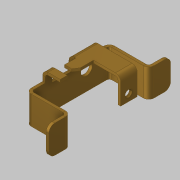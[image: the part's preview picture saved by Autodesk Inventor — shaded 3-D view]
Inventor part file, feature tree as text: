
AUTODESK INVENTOR PART (.ipt)
format: ipt  version: 2019 (Build 230136000, 136)  size: 312,832 bytes
history: native  units: mm
features: sheet_metal_op x9, sketch x9, other x6, extrude x3, hole x2, plane x2, chamfer x1
ambient origin geometry x8: Origin, YZ Plane, XZ Plane, XY Plane, X Axis, Y Axis, Z Axis, Center Point
bodies: Solid1 (feature_tree)
feature tree (32):
  sheet_metal_op  "Contour Flange1"
  chamfer  "Corner Round1"
  hole  "Hole1"  [1 undecoded]
  plane  "Work Plane1"
  sheet_metal_op  "Contour Flange2"
  plane  "Work Plane2"
  sheet_metal_op  "Contour Flange3"
  hole  "Hole2"  [1 undecoded]
  extrude  "Extrusion1"  Depth=3.0mm
  extrude  "Extrusion2"  Depth=6.0mm
  extrude  "Extrusion3"  Depth=32.0mm
  other  "Corner Chamfer1"
  other  "Definición del lado A"
  sketch  "Sketch1"  dims[d0=22.0mm d1=45.0mm]
  other  "Plate1"
  sheet_metal_op  "Bend1"
  sheet_metal_op  "Corner1"
  sketch  "Sketch2"  dims[d4=3.0mm d5=3.0mm]
  sketch  "Sketch5"  dims[d6=1.5mm d7=6.0mm]
  other  "Plate2"
  sheet_metal_op  "Bend2"
  sheet_metal_op  "Corner2"
  sketch  "Sketch6"  dims[d8=3.0mm d9=32.0mm]
  other  "Plate3"
  sheet_metal_op  "Bend3"
  sheet_metal_op  "Corner3"
  sketch  "Sketch7"  dims[d10=3.0mm]
  sketch  "Sketch8"  dims[d11=0.5mm]
  sketch  "Sketch9"  dims[d12=12.0mm]
  sketch  "Sketch10"  dims[d13=3.0mm d14=3.0mm d15=7.0mm d16=13.0mm d17=6.0mm d18=4.0mm d19=2.0mm d20=90.0deg d21=3.0mm d22=20.594885mm d23=22.0mm d25=-19.0mm d26=12.0mm d27=20.0mm d28=3.0mm d29=1.5mm d30=6.0mm d31=3.0mm d32=8.0mm d33=3.0mm d34=3.0mm d35=12.0mm d36=3.0mm d37=3.0mm d38=-49.0mm d39=12.0mm d41=51.0mm d42=30.0mm d43=3.0mm d44=1.5mm d45=6.0mm d46=3.0mm d47=27.0mm d48=3.0mm d49=3.0mm d50=12.0mm d51=3.0mm d52=3.0mm d53=8.0mm d54=6.0mm d55=4.0mm d56=2.0mm d57=90.0deg d58=3.0mm d59=20.594885mm d62=20.0mm d63=19.0mm d64=10.0mm d65=0.0mm d66=3.5mm d67=0.0mm d68=29.0mm d69=29.0mm d70=22.0mm d71=12.0mm d72=13.0mm d73=0.0mm d74=4.0mm d75=6.0mm d76=45.0deg]
  other  "Definición1"
  sketch  "Boceto1"  dims[d2=22.0mm d3=95.0mm]
note: 2 required parameter values undecoded (feature->parameter linkage not recoverable at this tier; creation-order binding heuristic only, values carry confidence <= 0.55)
